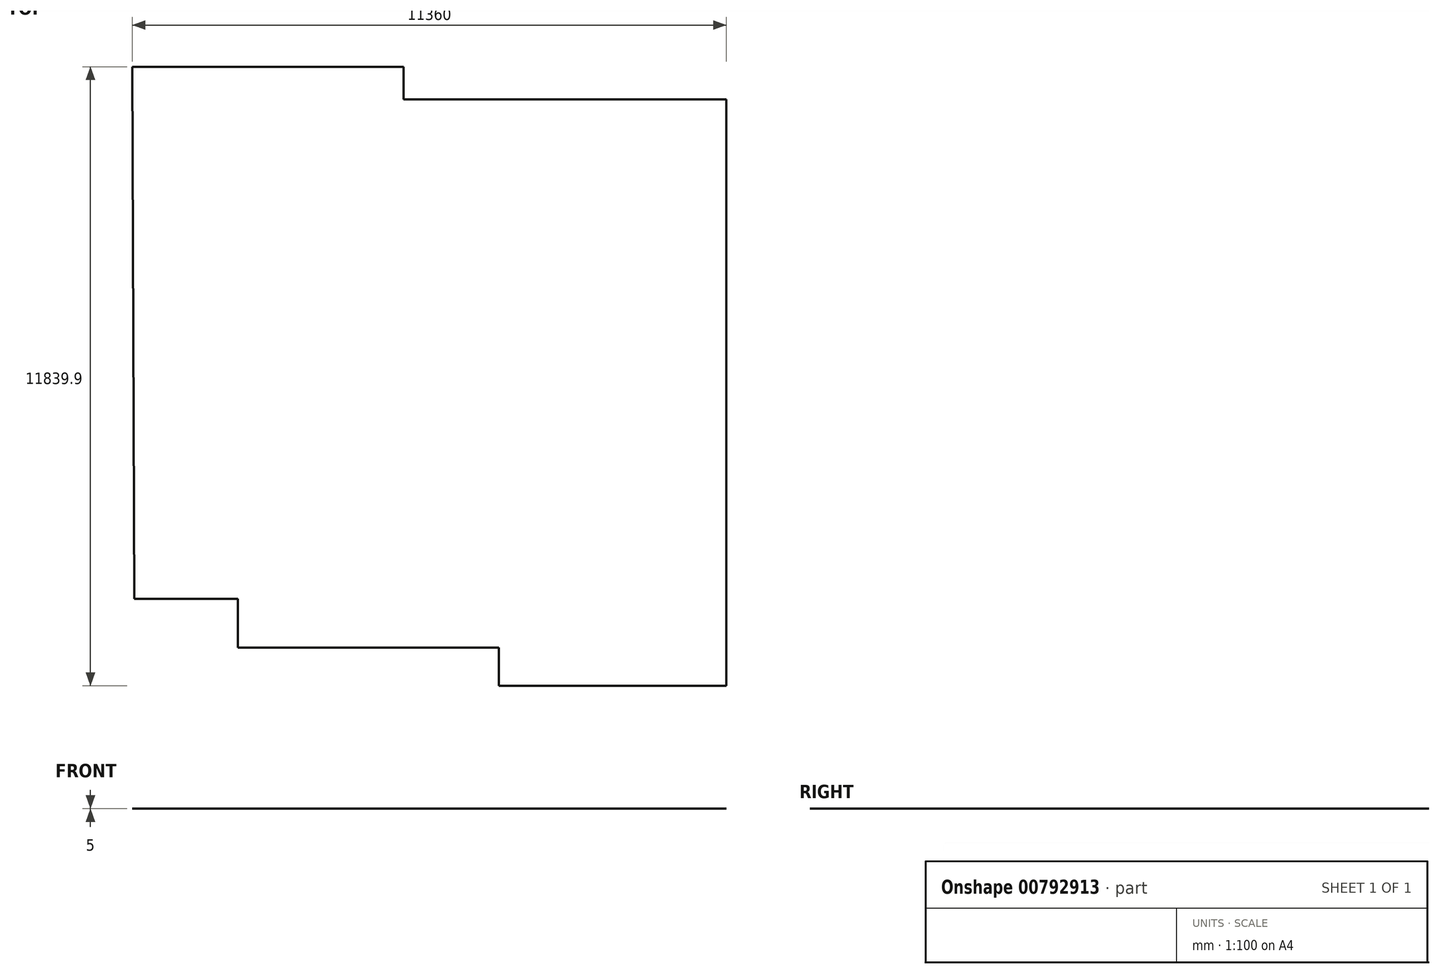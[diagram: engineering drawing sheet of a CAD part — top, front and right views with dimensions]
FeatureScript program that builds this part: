
annotation { "Feature Type Name" : "Feature", "Feature Type Description" : "" }
export const myFeature = defineFeature(function(context is Context, id is Id, definition is map)
    precondition{}
    {
        {
            var Q0;
            Q0=qCreatedBy(makeId("Top.planeOp"),FACE);
            var sketch = newSketch(context, id + "F0", { "sketchPlane" : qUnion([Q0])});
            skLineSegment(sketch, "E0.bottom", {"start": v(-17322.75, -3514.5) * mm, "end": v(2537.25, -3514.5) * mm});
            skLineSegment(sketch, "E0.top", {"start": v(-17322.75, -18644.5) * mm, "end": v(2537.25, -18644.5) * mm});
            skLineSegment(sketch, "E0.left", {"start": v(-17322.75, -3514.5) * mm, "end": v(-17322.75, -18644.5) * mm});
            skLineSegment(sketch, "E0.right", {"start": v(2537.25, -3514.5) * mm, "end": v(2537.25, -18644.5) * mm});
            skSolve(sketch);
        }
        {
            var Q0;
            Q0=makeQuery(id+"F0.imprint","IMPRINT",FACE,{"disambiguationData":[TD([[makeQuery(id+"F0.imprint","IMPRINT",EDGE,{"derivedFrom":sQuery(id+"F0.wireOp",EDGE,"E0.bottom")}),-1.0]])]});
            var sketch = newSketch(context, id + "F1", { "sketchPlane" : qUnion([Q0])});
            skLineSegment(sketch, "E1", {"start": v(-15392.75, -14664.43) * mm, "end": v(-13412.75, -14664.43) * mm});
            skLineSegment(sketch, "E2", {"start": v(-13412.75, -14664.43) * mm, "end": v(-13412.75, -15594.43) * mm});
            skLineSegment(sketch, "E3", {"start": v(-13412.75, -15594.43) * mm, "end": v(-8422.75, -15594.43) * mm});
            skLineSegment(sketch, "E4", {"start": v(-8422.75, -15594.43) * mm, "end": v(-8422.75, -16324.43) * mm});
            skLineSegment(sketch, "E5", {"start": v(-8422.75, -16324.43) * mm, "end": v(-4072.75, -16324.43) * mm});
            skLineSegment(sketch, "E6", {"start": v(-4072.75, -16324.43) * mm, "end": v(-4072.75, -5104.5) * mm});
            skLineSegment(sketch, "E7", {"start": v(-4072.75, -5104.5) * mm, "end": v(-10242.75, -5104.5) * mm});
            skLineSegment(sketch, "E8", {"start": v(-10242.75, -5104.5) * mm, "end": v(-10242.75, -4484.5) * mm});
            skLineSegment(sketch, "E9", {"start": v(-10242.75, -4484.5) * mm, "end": v(-15432.75, -4484.5) * mm});
            skLineSegment(sketch, "E10", {"start": v(-15432.75, -4484.5) * mm, "end": v(-15392.75, -14664.43) * mm});
            skSolve(sketch);
        }
        {
            var Q0;
            Q0 = qSketchRegion(id + "F1", true);
            extrude(context, id + "F2", {"entities" : qUnion([Q0]), "depth" : 5 * mm, "offsetDistance" : 25 * mm});
        }
    });
